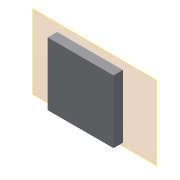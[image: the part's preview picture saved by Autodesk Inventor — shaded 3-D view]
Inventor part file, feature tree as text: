
AUTODESK INVENTOR PART (.ipt)
format: ipt  version: 2022 (Build 260153000, 153)  size: 135,168 bytes
history: native  units: in
note: dims shown in document units (in); Inventor stores cm internally (conversion verified against a paired STEP export)
features: other x5, extrude x3, sketch x3, reference x3, projected_geometry x2, plane x1
ambient origin geometry x8: Origin, YZ Plane, XZ Plane, XY Plane, X Axis, Y Axis, Z Axis, Center Point
bodies: Volumenkörper1 (feature_tree)
feature tree (17):
  plane  "Arbeitsebene1"
  extrude  "Extrusion1"  Depth=1.1811in
  extrude  "Extrusion2"  Depth=0.1929in
  extrude  "Extrusion3"  Depth=0.1575in TaperAngle=0.0deg
  sketch  "Skizze1"  dims[d0=1.1811in d1=1.1811in]
  reference  "Referenz1"
  sketch  "Skizze2"  dims[d2=0.1929in d3=0.1929in]
  projected_geometry  "Projizierte Kontur1"
  sketch  "Skizze3"  dims[d4=0.1929in d5=0.1575in d6=0.0in d7=0.0394in d8=0.0in d9=0.8225in d10=0.4113in d11=0.1969in d12=0.7874in d13=0.0in]
  projected_geometry  "Projizierte Kontur2"
  reference  "Referenz2"
  reference  "Referenz3"
  other  "<userpath>\Documents\GitHub\cellstorm\INVENTOR\cellSTORM_v6.iam"
  other  "cellSTORM_v6.iam"
  other  "cellSTORM_v5_laserstage:1"
  other  "cellSTORM_v5_microsocpe:1"
  other  "cellSTORM_lightpath:2"
